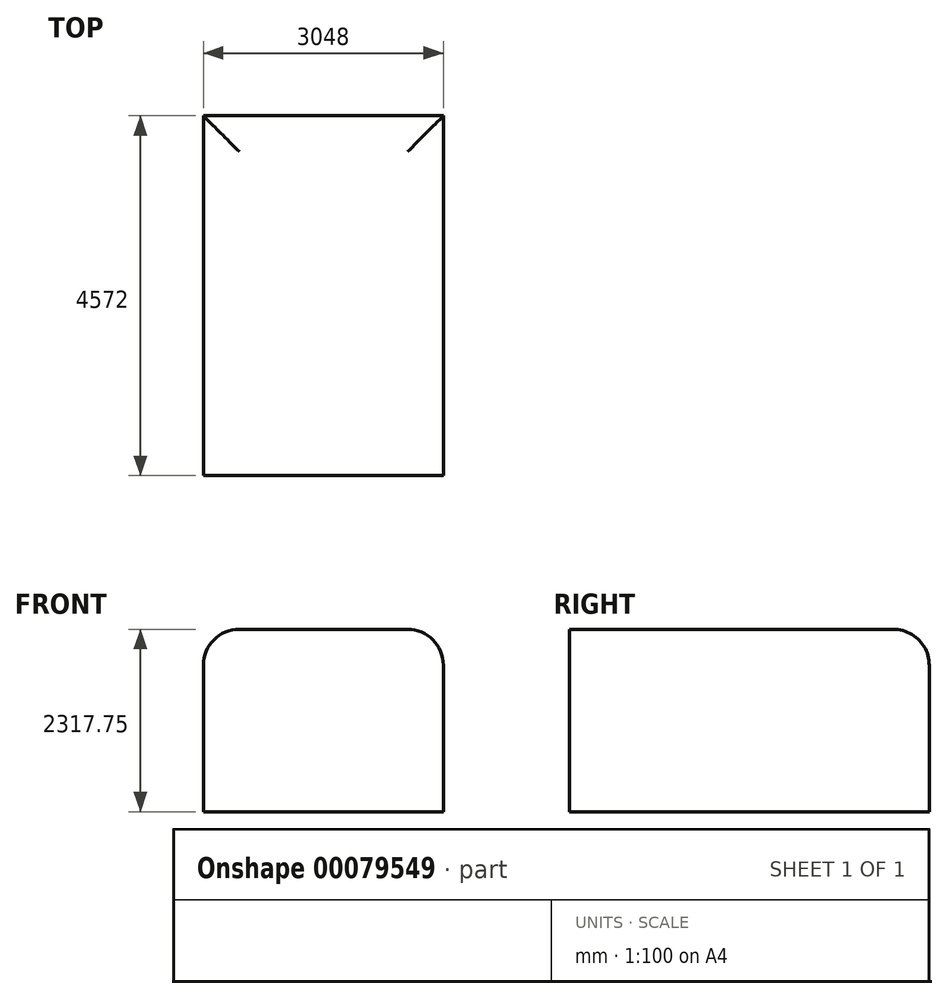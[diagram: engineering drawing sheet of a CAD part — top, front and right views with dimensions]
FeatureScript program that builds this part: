
annotation { "Feature Type Name" : "Feature", "Feature Type Description" : "" }
export const myFeature = defineFeature(function(context is Context, id is Id, definition is map)
    precondition{}
    {
        {
            var Q0;
            Q0=qCreatedBy(makeId("Top.planeOp"),FACE);
            var sketch = newSketch(context, id + "F0", { "sketchPlane" : qUnion([Q0])});
            skLineSegment(sketch, "E0.bottom", {"start": v(1524, 2286) * mm, "end": v(-1524, 2286) * mm});
            skLineSegment(sketch, "E0.top", {"start": v(1524, -2286) * mm, "end": v(-1524, -2286) * mm});
            skLineSegment(sketch, "E0.left", {"start": v(1524, 2286) * mm, "end": v(1524, -2286) * mm});
            skLineSegment(sketch, "E0.right", {"start": v(-1524, 2286) * mm, "end": v(-1524, -2286) * mm});
            skPoint(sketch, "E0.middle", {"position": v(0, 0) * mm});
            skSolve(sketch);
        }
        {
            var Q0;
            Q0=makeQuery(id+"F0.imprint","IMPRINT",FACE,{"disambiguationData":[TD([[makeQuery(id+"F0.imprint","IMPRINT",EDGE,{"derivedFrom":sQuery(id+"F0.wireOp",EDGE,"E0.bottom")}),1.0]])]});
            extrude(context, id + "F1", {"entities" : qUnion([Q0]), "endBound" : BoundingType.SYMMETRIC, "depth" : 2133.6 * mm});
        }
        {
            var Q0;
            Q0=makeQuery(id+"F1.opExtrude","CAP_FACE",FACE,{"disambiguationData":[OSD([sQuery(id+"F0.wireOp",EDGE,"E0.bottom"),sQuery(id+"F0.wireOp",EDGE,"E0.top"),sQuery(id+"F0.wireOp",EDGE,"E0.left"),sQuery(id+"F0.wireOp",EDGE,"E0.right")])],"isStart":true});
            extrude(context, id + "F2", {"entities" : qUnion([Q0]), "operationType" : NewBodyOperationType.ADD, "endBound" : BoundingType.SYMMETRIC, "depth" : 304.8 * mm});
        }
        {
            var Q0;
            Q0=makeQuery(id+"F2.opExtrude","CAP_FACE",FACE,{"disambiguationData":[OSD([sQuery(id+"F0.wireOp",EDGE,"E0.bottom"),sQuery(id+"F0.wireOp",EDGE,"E0.top"),sQuery(id+"F0.wireOp",EDGE,"E0.left"),sQuery(id+"F0.wireOp",EDGE,"E0.right")])],"isStart":false});
            extrude(context, id + "F3", {"entities" : qUnion([Q0]), "operationType" : NewBodyOperationType.ADD, "endBound" : BoundingType.SYMMETRIC, "depth" : 50.8 * mm});
        }
        {
            var Q0;
            Q0=makeQuery(id+"F3.opExtrude","CAP_FACE",FACE,{"disambiguationData":[OSD([sQuery(id+"F0.wireOp",EDGE,"E0.bottom"),sQuery(id+"F0.wireOp",EDGE,"E0.top"),sQuery(id+"F0.wireOp",EDGE,"E0.left"),sQuery(id+"F0.wireOp",EDGE,"E0.right")])],"isStart":false});
            extrude(context, id + "F4", {"entities" : qUnion([Q0]), "operationType" : NewBodyOperationType.ADD, "endBound" : BoundingType.SYMMETRIC, "depth" : 12.7 * mm});
        }
        {
            var Q0;
            Q0=makeQuery(id+"F1.opExtrude","CAP_EDGE",EDGE,{"disambiguationData":[OSD([sQuery(id+"F0.wireOp",EDGE,"E0.right")])],"isStart":false});
            var Q1;
            Q1=makeQuery(id+"F1.opExtrude","CAP_EDGE",EDGE,{"disambiguationData":[OSD([sQuery(id+"F0.wireOp",EDGE,"E0.left")])],"isStart":false});
            var Q2;
            Q2=makeQuery(id+"F1.opExtrude","CAP_EDGE",EDGE,{"disambiguationData":[OSD([sQuery(id+"F0.wireOp",EDGE,"E0.bottom")])],"isStart":false});
            fillet(context, id + "F5", {"entities" : qUnion([Q0, Q1, Q2]), "radius" : 457.2 * mm, "tangentPropagation" : true, "allowEdgeOverflow" : false});
        }
    });
